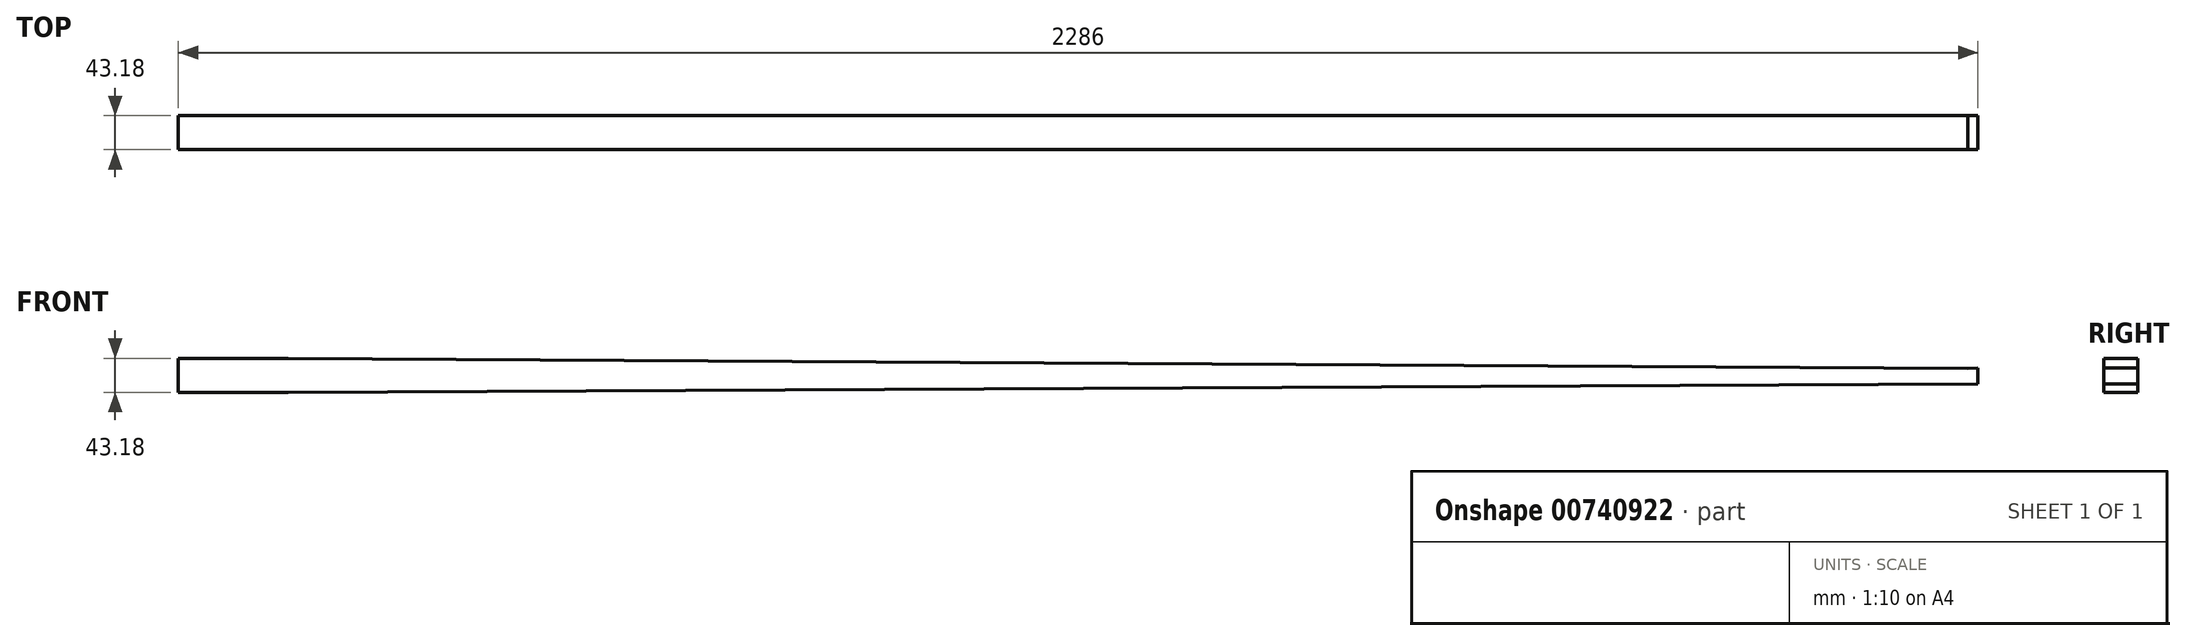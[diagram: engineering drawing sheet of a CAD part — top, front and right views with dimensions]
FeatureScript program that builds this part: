
annotation { "Feature Type Name" : "Feature", "Feature Type Description" : "" }
export const myFeature = defineFeature(function(context is Context, id is Id, definition is map)
    precondition{}
    {
        {
            var Q0;
            Q0=qCreatedBy(makeId("Front.planeOp"),FACE);
            var sketch = newSketch(context, id + "F0", { "sketchPlane" : qUnion([Q0])});
            skLineSegment(sketch, "E0", {"start": v(0, 0) * mm, "end": v(0, 43.18) * mm});
            skLineSegment(sketch, "E1", {"start": v(2133.6, 10.16) * mm, "end": v(0, 0) * mm});
            skLineSegment(sketch, "E2", {"start": v(2133.6, 10.16) * mm, "end": v(2133.5, 30.48) * mm});
            skLineSegment(sketch, "E3", {"start": v(2133.5, 30.48) * mm, "end": v(0, 43.18) * mm});
            skSolve(sketch);
        }
        {
            var Q0;
            Q0 = qSketchRegion(id + "F0", true);
            extrude(context, id + "F1", {"entities" : qUnion([Q0]), "depth" : 43.18 * mm, "offsetDistance" : 25.4 * mm});
        }
        {
            var Q0;
            Q0=makeQuery(id+"F1.opExtrude","SWEPT_FACE",FACE,{"disambiguationData":[OSD([sQuery(id+"F0.wireOp",EDGE,"E0")])]});
            var sketch = newSketch(context, id + "F2", { "sketchPlane" : qUnion([Q0])});
            skLineSegment(sketch, "E4.bottom", {"start": v(0, 43.18) * mm, "end": v(43.18, 43.18) * mm});
            skLineSegment(sketch, "E4.top", {"start": v(0, 0) * mm, "end": v(43.18, 0) * mm});
            skLineSegment(sketch, "E4.left", {"start": v(0, 43.18) * mm, "end": v(0, 0) * mm});
            skLineSegment(sketch, "E4.right", {"start": v(43.18, 43.18) * mm, "end": v(43.18, 0) * mm});
            skSolve(sketch);
        }
        {
            var Q0;
            Q0 = qSketchRegion(id + "F2", true);
            extrude(context, id + "F3", {"entities" : qUnion([Q0]), "operationType" : NewBodyOperationType.ADD, "depth" : 139.7 * mm, "offsetDistance" : 25.4 * mm});
        }
        {
            var Q0;
            Q0=makeQuery(id+"F1.opExtrude","SWEPT_FACE",FACE,{"disambiguationData":[OSD([sQuery(id+"F0.wireOp",EDGE,"E2")])]});
            var sketch = newSketch(context, id + "F4", { "sketchPlane" : qUnion([Q0])});
            skLineSegment(sketch, "E5.bottom", {"start": v(-43.18, 20.32) * mm, "end": v(0, 20.32) * mm});
            skLineSegment(sketch, "E5.top", {"start": v(-43.18, 0) * mm, "end": v(0, 0) * mm});
            skLineSegment(sketch, "E5.left", {"start": v(-43.18, 20.32) * mm, "end": v(-43.18, 0) * mm});
            skLineSegment(sketch, "E5.right", {"start": v(0, 20.32) * mm, "end": v(0, 0) * mm});
            skSolve(sketch);
        }
        {
            var Q0;
            Q0 = qSketchRegion(id + "F4", true);
            extrude(context, id + "F5", {"entities" : qUnion([Q0]), "operationType" : NewBodyOperationType.ADD, "depth" : 12.7 * mm, "offsetDistance" : 25.4 * mm});
        }
    });
